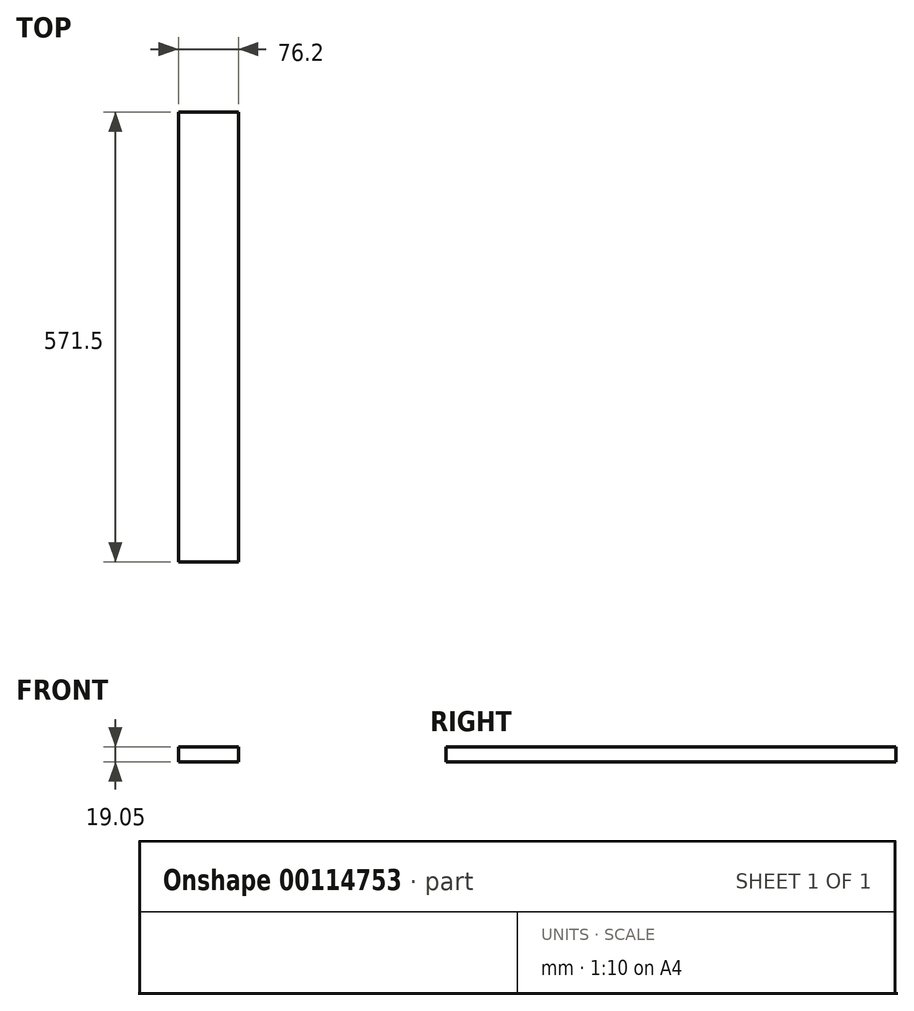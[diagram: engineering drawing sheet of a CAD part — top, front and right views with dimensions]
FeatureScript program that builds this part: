
annotation { "Feature Type Name" : "Feature", "Feature Type Description" : "" }
export const myFeature = defineFeature(function(context is Context, id is Id, definition is map)
    precondition{}
    {
        {
            var Q0;
            Q0=qCreatedBy(makeId("Top.planeOp"),FACE);
            var sketch = newSketch(context, id + "F0", { "sketchPlane" : qUnion([Q0])});
            skLineSegment(sketch, "E0.bottom", {"start": v(0, 0) * mm, "end": v(76.2, 0) * mm});
            skLineSegment(sketch, "E0.top", {"start": v(0, 571.5) * mm, "end": v(76.2, 571.5) * mm});
            skLineSegment(sketch, "E0.left", {"start": v(0, 0) * mm, "end": v(0, 571.5) * mm});
            skLineSegment(sketch, "E0.right", {"start": v(76.2, 0) * mm, "end": v(76.2, 571.5) * mm});
            skSolve(sketch);
        }
        {
            var Q0;
            Q0=qSketchRegion(id+"F0",true);
            extrude(context, id + "F1", {"entities" : qUnion([Q0]), "depth" : 19.05 * mm});
        }
    });
